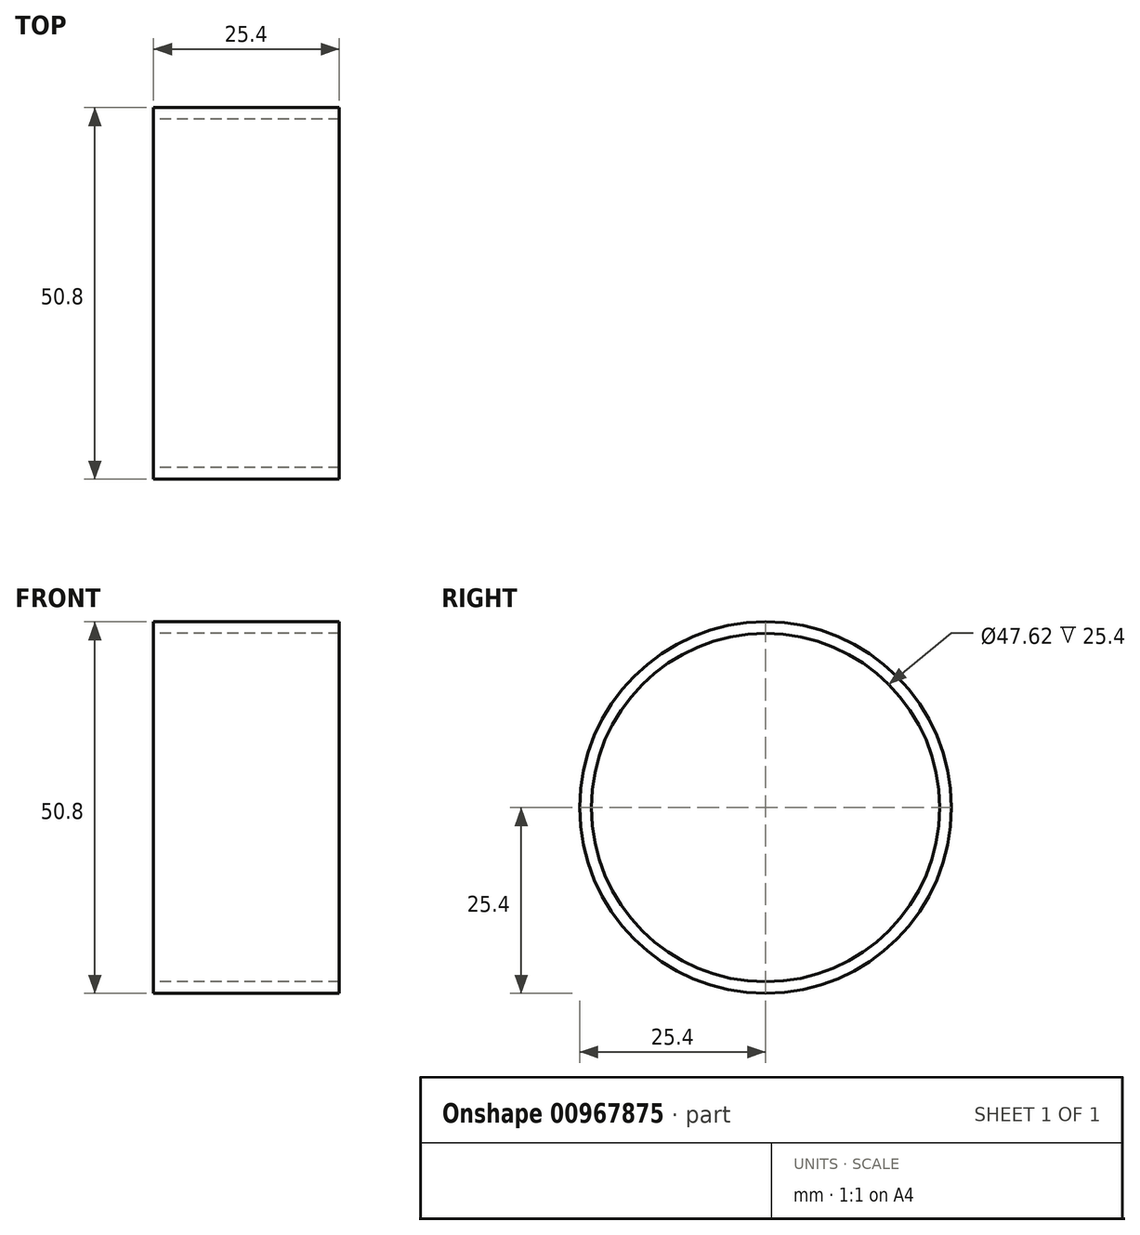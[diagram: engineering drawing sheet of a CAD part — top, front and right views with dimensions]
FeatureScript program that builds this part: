
annotation { "Feature Type Name" : "Feature", "Feature Type Description" : "" }
export const myFeature = defineFeature(function(context is Context, id is Id, definition is map)
    precondition{}
    {
        {
            var Q0;
            Q0=qCreatedBy(makeId("Right.planeOp"),FACE);
            var sketch = newSketch(context, id + "F0", { "sketchPlane" : qUnion([Q0])});
            skCircle(sketch, "E0", {"center": v(0, 0) * mm, "radius": 25.4 * mm});
            skCircle(sketch, "E1", {"center": v(0, 0) * mm, "radius": 23.81 * mm});
            skPoint(sketch, "E2", {"position": v(0, 23.81) * mm});
            skPoint(sketch, "E3", {"position": v(0, 25.4) * mm});
            skSolve(sketch);
        }
        {
            var Q0;
            Q0=makeQuery(id+"F0.imprint","IMPRINT",FACE,{"disambiguationData":[TD([[makeQuery(id+"F0.imprint","IMPRINT",EDGE,{"derivedFrom":sQuery(id+"F0.wireOp",EDGE,"E0")}),1.0]])]});
            extrude(context, id + "F1", {"entities" : qUnion([Q0]), "endBound" : BoundingType.SYMMETRIC, "depth" : 25.4 * mm, "offsetDistance" : 25.4 * mm});
        }
    });
